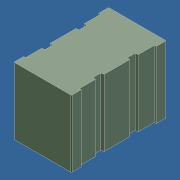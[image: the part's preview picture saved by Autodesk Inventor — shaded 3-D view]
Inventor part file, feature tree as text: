
AUTODESK INVENTOR PART (.ipt)
format: ipt  version: 2014 (Build 180170000, 170)  size: 143,360 bytes
history: native  units: in
note: dims shown in document units (in); Inventor stores cm internally (conversion verified against a paired STEP export)
features: other x21, extrude x3, sketch x3, pattern_linear x1
ambient origin geometry x8: Origin, YZ Plane, XZ Plane, XY Plane, X Axis, Y Axis, Z Axis, Center Point
bodies: Solid1 (feature_tree)
feature tree (28):
  extrude  "Extrusion1"  Depth=0.001in TaperAngle=0.0deg
  extrude  "Extrusion2"  Depth=0.185in TaperAngle=0.0deg
  extrude  "Extrusion3"  [1 undecoded]
  pattern_linear  "Rectangular Pattern1"  [2 undecoded]
  other  "rot_XY"
  other  "rot_YZ"
  other  "rot_ZX"
  other  "rot_X"
  other  "rot_Y"
  other  "rot_Z"
  other  "rot_Center"
  other  "to_cover_XY"
  other  "to_cover_YZ"
  other  "to_cover_ZX"
  other  "to_cover_X"
  other  "to_cover_Y"
  other  "to_cover_Z"
  other  "to_cover_Center"
  other  "to_terminals_XY"
  other  "to_terminals_YZ"
  other  "to_terminals_ZX"
  other  "to_terminals_X"
  other  "to_terminals_Y"
  other  "to_terminals_Z"
  other  "to_terminals_Center"
  sketch  "Sketch_2"  dims[d4=0.01in d5=0.0in d6=1.1811in d8=0.185in d9=0.3937in d11=0.0in]
  sketch  "Sketch_1"  dims[d0=0.361in d1=0.0in d2=0.001in d3=0.0in]
  sketch  "Sketch_7"
note: 3 required parameter values undecoded (feature->parameter linkage not recoverable at this tier; creation-order binding heuristic only, values carry confidence <= 0.55)
